# Revit family: Single Skin Roofing_Brownie Blanket (STC 28_Uvalue 0.62)
name_source: partatom
category: Generic Models
units: mm (PartAtom-declared; Revit-internal decimal feet)

## family parameters
Can host rebar = No
Cut with Voids When Loaded = No
Host = Face
Part Type = Normal
Room Calculation Point = No
Round Connector Dimension = Use Diameter
Shared = No

## types (3) — shared parameters
Actual Width (mm) = 3000 mm  [stored 9.84252 ft]
Aluminium foil = Aluminium foil (Double Sided)
ArrayNum = 3
ArrayNum (Top Skin) = 9
Description = ECOWOOL Brownie blanket and slabs are resilient, non-combustible, glass mineral wool products, supplied at roofing and walling application for residential and commercial building
Insulation = BROWNIE BLANKET
Length (mm) = 2000 mm  [stored 6.56168 ft]
Length Insulation = 2000 mm  [stored 6.56168 ft]
Manufacturer = PGF Insulation Sdn. Bhd.
ProVisSingle (Top Skin) = No
ProfArrN = 3
ProfArrN (Top Skin) = 9
ProfVisDouble = Yes
ProfVisDouble (Top Skin) = Yes
ProfVisSingle = No
SubL = 2805 mm  [stored 9.20276 ft]
SubL (Top Skin) = 2718 mm  [stored 8.91732 ft]
SubW = 3740 mm
SubW (Top Skin) = 3020 mm  [stored 9.90814 ft]
Thermal K Value = 0.0342
Type of Insulation = Glass Mineral Wool Blanket
URL = www.ecowool.com.my
zero-valued in all types: Default Elevation

## per-type parameters (varying)
| type | A | ECOWOOL Product thickness in mm | Finish | Insulation Density | Insulation Density (kg/m3) | Insulation thk. (mm) | Remarks | STC No | STC in dB | System Description | Thermal R Value | Total System Thickness-mm | Typical weight of ECOWOOL-Kg/M2 | U-Value W/m2k |
| 75mm | 76.5 mm  [stored 0.250984 ft] |  | ZINCALUME® ULTRA -  ACTIVATE™ | 16 kg/m³ | 32 mm  [stored 0.104987 ft] | 75 mm |  |  | 0 |  | 2.19 | 0 mm  [stored 0 ft] | 0 mm  [stored 0 ft] | 0 mm  [stored 0 ft] |
| 50mm | 51.5 mm  [stored 0.168963 ft] |  | ZINCALUME® ULTRA -  ACTIVATE™ | 24 kg/m³ | 32 mm  [stored 0.104987 ft] | 50 mm  [stored 0.164042 ft] |  |  | 0 |  | 1.46 | 0 mm  [stored 0 ft] | 0 mm  [stored 0 ft] | 0 mm  [stored 0 ft] |
| ECOWOOL EWBL1.45 | 51.5 mm  [stored 0.168963 ft] | 50mm x 24 Kg/m3 | Meta Deck Roofing | 24 kg/m³ | 24 mm  [stored 0.0787402 ft] | 50 mm  [stored 0.164042 ft] | Single skin metal roof for food centre
or canteen, low cost warehouses, usually non air-condition,
without walls and highly ventilated
environment. Also commonly used
in walkways and common pavilion
in residential estates | STC 28 | 28 | 1. Aluminum Foil
2. Ecowool  EWBL1.45
3. Metal Deck/ Zincalume Liner | 1.45 | 52.95 mm  [stored 0.17372 ft] | 1.2 mm  [stored 0.00393701 ft] | 0.62 mm  [stored 0.00203412 ft] |

note: [stored X ft] marks values corroborated as IEEE doubles in the binary element streams (Revit-internal decimal feet)

## geometry (parser evidence)
native form markers: Sweep x26
no freeform markers — native parametric forms only
